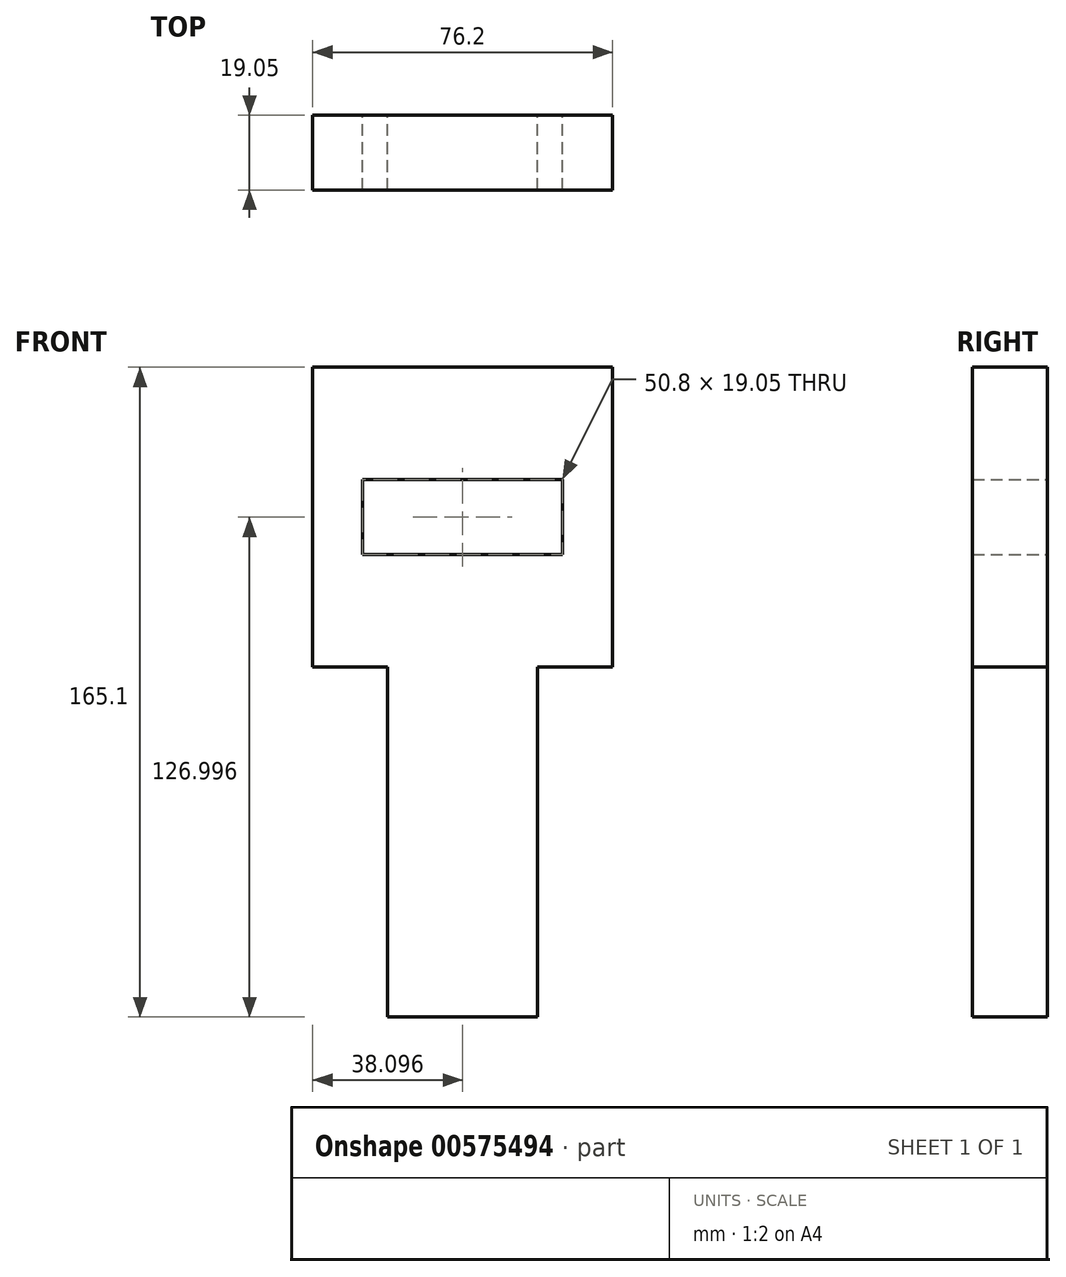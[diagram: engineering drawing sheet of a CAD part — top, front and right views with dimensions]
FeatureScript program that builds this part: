
annotation { "Feature Type Name" : "Feature", "Feature Type Description" : "" }
export const myFeature = defineFeature(function(context is Context, id is Id, definition is map)
    precondition{}
    {
        {
            var Q0;
            Q0=qCreatedBy(makeId("Front.planeOp"),FACE);
            var sketch = newSketch(context, id + "F0", { "sketchPlane" : qUnion([Q0])});
            skLineSegment(sketch, "E0.bottom", {"start": v(-201.54, -7.94) * mm, "end": v(-163.44, -7.94) * mm});
            skLineSegment(sketch, "E0.top", {"start": v(-201.54, -134.94) * mm, "end": v(-163.44, -134.94) * mm});
            skLineSegment(sketch, "E0.left", {"start": v(-201.54, -7.94) * mm, "end": v(-201.54, -134.94) * mm});
            skLineSegment(sketch, "E0.right", {"start": v(-163.44, -7.94) * mm, "end": v(-163.44, -134.94) * mm});
            skLineSegment(sketch, "E1.bottom", {"start": v(-144.4, 30.16) * mm, "end": v(-220.6, 30.16) * mm});
            skLineSegment(sketch, "E1.top", {"start": v(-144.4, -46.04) * mm, "end": v(-220.6, -46.04) * mm});
            skLineSegment(sketch, "E1.left", {"start": v(-144.4, 30.16) * mm, "end": v(-144.4, -46.04) * mm});
            skLineSegment(sketch, "E1.right", {"start": v(-220.6, 30.16) * mm, "end": v(-220.6, -46.04) * mm});
            skPoint(sketch, "E1.middle", {"position": v(-182.5, -7.94) * mm});
            skLineSegment(sketch, "E2.bottom", {"start": v(-157.1, 1.58) * mm, "end": v(-207.9, 1.58) * mm});
            skLineSegment(sketch, "E2.top", {"start": v(-157.1, -17.47) * mm, "end": v(-207.9, -17.47) * mm});
            skLineSegment(sketch, "E2.left", {"start": v(-157.1, 1.58) * mm, "end": v(-157.1, -17.47) * mm});
            skLineSegment(sketch, "E2.right", {"start": v(-207.9, 1.58) * mm, "end": v(-207.9, -17.47) * mm});
            skSolve(sketch);
        }
        {
            var Q0;
            Q0=makeQuery(id+"F0.imprint","IMPRINT",FACE,{"disambiguationData":[TD([[makeQuery(id+"F0.imprint","IMPRINT",EDGE,{"derivedFrom":sQuery(id+"F0.wireOp",EDGE,"E1.bottom")}),1.0]])]});
            var Q1;
            {var subQ0=sQuery(id+"F0.wireOp",EDGE,"E1.top");var subQ1=sQuery(id+"F0.wireOp",EDGE,"E0.left");var subQ2=makeQuery(id+"F0.imprint","INTERSECT",VERTEX,{"derivedFrom":[subQ1,subQ0]});Q1=makeQuery(id+"F0.imprint","IMPRINT",FACE,{"disambiguationData":[TD([[makeQuery(id+"F0.imprint","IMPRINT",EDGE,{"disambiguationData":[TD([[subQ2,1.0]])],"derivedFrom":subQ1}),1.0]])]});}
            var Q2;
            {var subQ0=sQuery(id+"F0.wireOp",EDGE,"E0.top");Q2=makeQuery(id+"F0.imprint","IMPRINT",FACE,{"disambiguationData":[TD([[makeQuery(id+"F0.imprint","IMPRINT",EDGE,{"derivedFrom":subQ0}),1.0]])]});}
            extrude(context, id + "F1", {"entities" : qUnion([Q0, Q1, Q2]), "depth" : 19.05 * mm, "offsetDistance" : 25.4 * mm});
        }
    });
